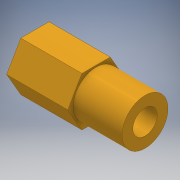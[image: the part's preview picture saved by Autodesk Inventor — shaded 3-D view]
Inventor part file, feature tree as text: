
AUTODESK INVENTOR PART (.ipt)
format: ipt  version: 2018.2 (Build 222227000, 227)  size: 119,296 bytes
history: native  units: mm
features: sketch x3, extrude x2, hole x2, other x1, thread x1
ambient origin geometry x8: Origin, YZ Plane, XZ Plane, XY Plane, X Axis, Y Axis, Z Axis, Center Point
bodies: Body1 (feature_tree)
feature tree (9):
  other  "ソリッド1"
  extrude  "押し出し1"  Depth=10.0mm TaperAngle=0.0deg
  extrude  "押し出し2"  Depth=7.5mm
  hole  "穴1"  [1 undecoded]
  hole  "穴2"  [1 undecoded]
  thread  "ねじ1"
  sketch  "3D スケッチ1"
  sketch  "スケッチ1"
  sketch  "スケッチ2"
note: 2 required parameter values undecoded (feature->parameter linkage not recoverable at this tier; creation-order binding heuristic only, values carry confidence <= 0.55)
